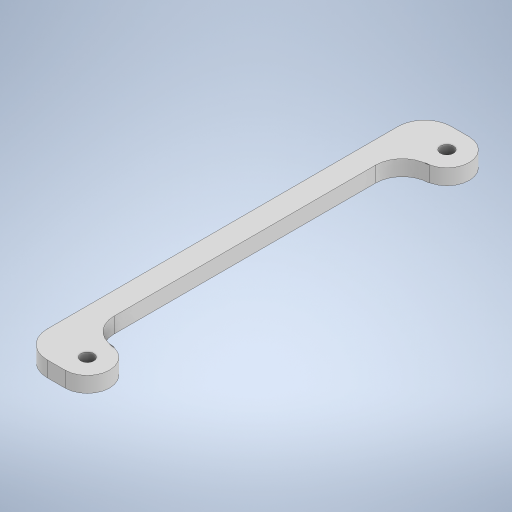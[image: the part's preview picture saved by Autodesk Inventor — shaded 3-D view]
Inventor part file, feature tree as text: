
AUTODESK INVENTOR PART (.ipt)
format: ipt  version: 2023 (Build 270158000, 158)  size: 254,464 bytes
history: native  units: in
note: dims shown in document units (in); Inventor stores cm internally (conversion verified against a paired STEP export)
features: extrude x1, sketch x1
ambient origin geometry x8: Origin, YZ Plane, XZ Plane, XY Plane, X Axis, Y Axis, Z Axis, Center Point
bodies: Solid1 (feature_tree)
feature tree (2):
  extrude  "Extrusion1"  Depth=0.1378in
  sketch  "Sketch1"  dims[d0=0.116in d2=0.116in d3=0.395in d4=0.395in d7=3.187in d8=0.395in d9=0.2362in d10=0.2362in d11=0.2362in d12=0.2362in d13=0.1378in d14=0.0in]
